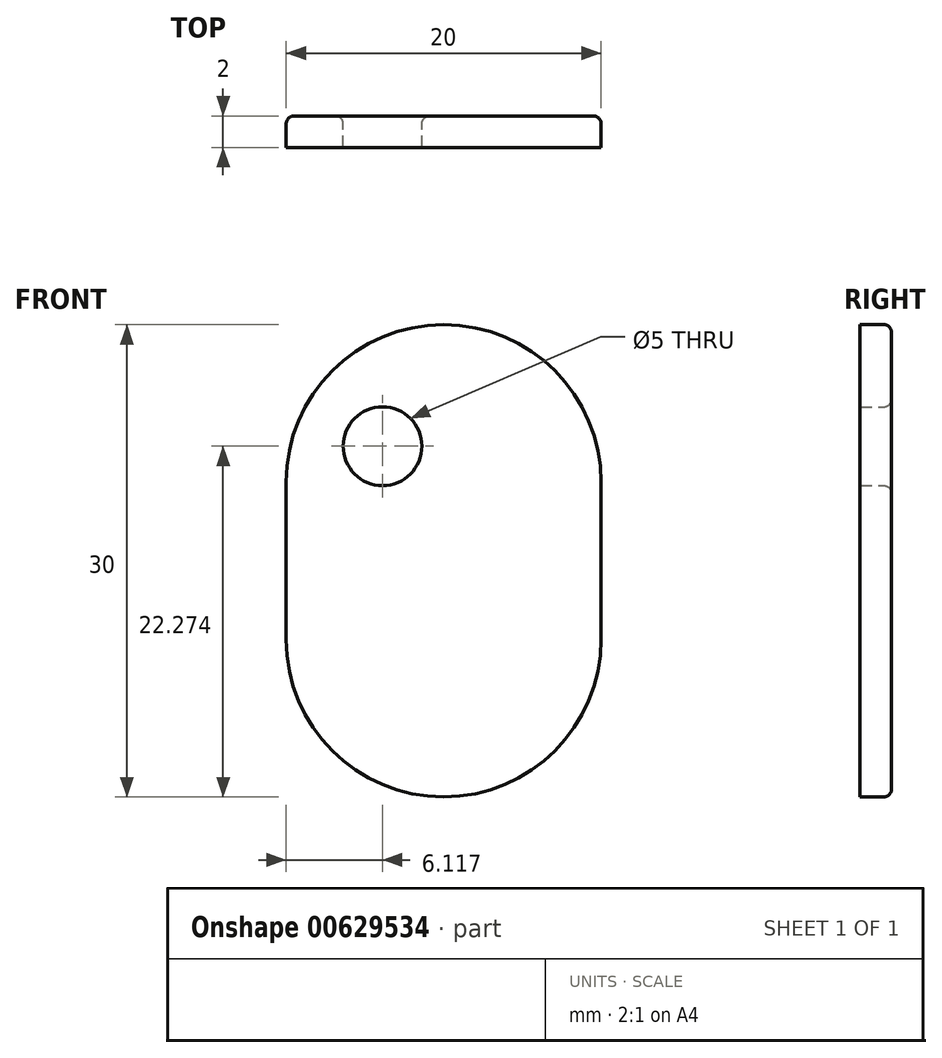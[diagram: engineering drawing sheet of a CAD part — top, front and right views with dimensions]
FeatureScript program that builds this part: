
annotation { "Feature Type Name" : "Feature", "Feature Type Description" : "" }
export const myFeature = defineFeature(function(context is Context, id is Id, definition is map)
    precondition{}
    {
        {
            var Q0;
            Q0=qCreatedBy(makeId("Front.planeOp"),FACE);
            var sketch = newSketch(context, id + "F0", { "sketchPlane" : qUnion([Q0])});
            skLineSegment(sketch, "E0.bottom", {"start": v(8.61, 19.68) * mm, "end": v(8.61, 19.68) * mm});
            skLineSegment(sketch, "E0.top", {"start": v(8.61, -10.32) * mm, "end": v(8.61, -10.32) * mm});
            skLineSegment(sketch, "E0.left", {"start": v(-1.39, 9.68) * mm, "end": v(-1.39, -0.32) * mm});
            skLineSegment(sketch, "E0.right", {"start": v(18.61, 9.68) * mm, "end": v(18.61, -0.32) * mm});
            skPoint(sketch, "E1.visualSharp", {"position": v(18.61, -10.32) * mm});
            skArc(sketch, "E1.filletArc", {"start": v(8.61, -10.32) * mm, "mid": v(15.68, -7.4) * mm, "end": v(18.61, -0.32) * mm});
            skPoint(sketch, "E2.visualSharp", {"position": v(-1.39, -10.32) * mm});
            skArc(sketch, "E2.filletArc", {"start": v(-1.39, -0.32) * mm, "mid": v(1.54, -7.4) * mm, "end": v(8.61, -10.32) * mm});
            skPoint(sketch, "E3.visualSharp", {"position": v(-1.39, 19.68) * mm});
            skArc(sketch, "E3.filletArc", {"start": v(8.61, 19.68) * mm, "mid": v(1.54, 16.75) * mm, "end": v(-1.39, 9.68) * mm});
            skPoint(sketch, "E4.visualSharp", {"position": v(18.61, 19.68) * mm});
            skArc(sketch, "E4.filletArc", {"start": v(18.61, 9.68) * mm, "mid": v(15.68, 16.75) * mm, "end": v(8.61, 19.68) * mm});
            skCircle(sketch, "E5", {"center": v(4.73, 11.95) * mm, "radius": 2.5 * mm});
            skSolve(sketch);
        }
        {
            var Q0;
            Q0=makeQuery(id+"F0.imprint","IMPRINT",FACE,{"disambiguationData":[TD([[makeQuery(id+"F0.imprint","IMPRINT",EDGE,{"derivedFrom":sQuery(id+"F0.wireOp",EDGE,"E0.left")}),1.0]])]});
            extrude(context, id + "F1", {"entities" : qUnion([Q0]), "depth" : 2 * mm, "offsetDistance" : 25 * mm});
        }
        {
            var Q0;
            Q0=makeQuery(id+"F1.opExtrude","CAP_FACE",FACE,{"disambiguationData":[OSD([sQuery(id+"F0.wireOp",EDGE,"E0.left"),sQuery(id+"F0.wireOp",EDGE,"E0.right"),sQuery(id+"F0.wireOp",EDGE,"E1.filletArc"),sQuery(id+"F0.wireOp",EDGE,"E2.filletArc"),sQuery(id+"F0.wireOp",EDGE,"E3.filletArc"),sQuery(id+"F0.wireOp",EDGE,"E4.filletArc"),sQuery(id+"F0.wireOp",EDGE,"E5")])],"isStart":true});
            fillet(context, id + "F2", {"entities" : qUnion([Q0]), "radius" : 0.5 * mm, "tangentPropagation" : true, "allowEdgeOverflow" : false});
        }
    });
